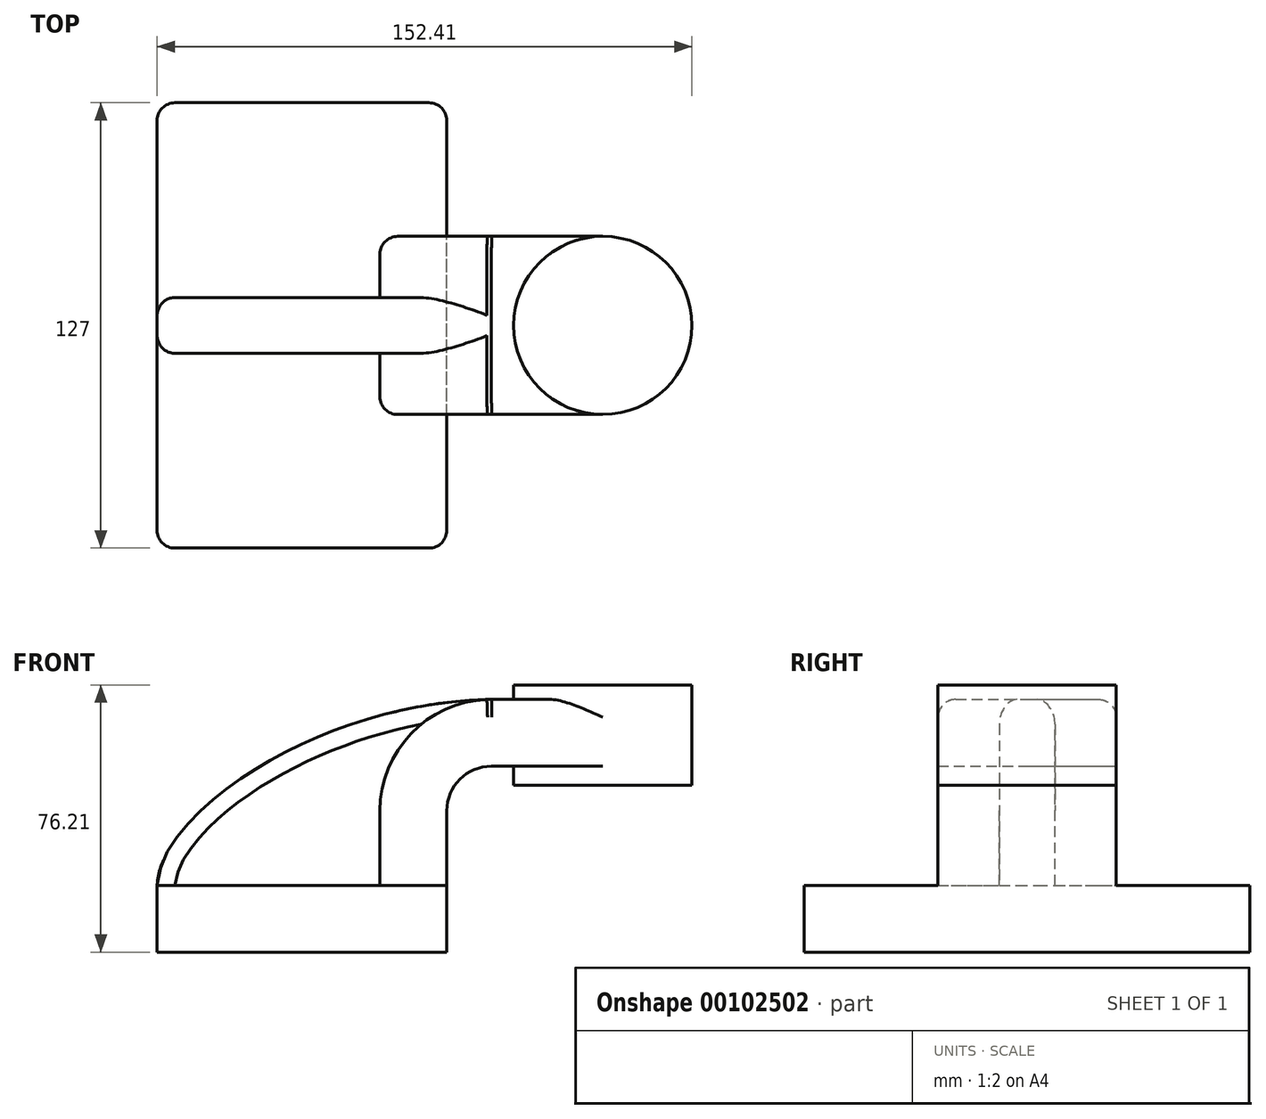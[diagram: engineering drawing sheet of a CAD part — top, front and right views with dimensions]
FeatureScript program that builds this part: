
annotation { "Feature Type Name" : "Feature", "Feature Type Description" : "" }
export const myFeature = defineFeature(function(context is Context, id is Id, definition is map)
    precondition{}
    {
        {
            var Q0;
            Q0=qCreatedBy(makeId("Front.planeOp"),FACE);
            var sketch = newSketch(context, id + "F0", { "sketchPlane" : qUnion([Q0])});
            skLineSegment(sketch, "E0.bottom", {"start": v(41.28, -9.52) * mm, "end": v(-41.28, -9.53) * mm});
            skLineSegment(sketch, "E0.top", {"start": v(41.28, 9.53) * mm, "end": v(-41.28, 9.53) * mm});
            skLineSegment(sketch, "E0.left", {"start": v(41.28, -9.52) * mm, "end": v(41.28, 9.53) * mm});
            skLineSegment(sketch, "E0.right", {"start": v(-41.28, -9.53) * mm, "end": v(-41.28, 9.53) * mm});
            skPoint(sketch, "E0.middle", {"position": v(0, 0) * mm});
            skLineSegment(sketch, "E1.bottom", {"start": v(111.12, 38.1) * mm, "end": v(60.33, 38.1) * mm});
            skLineSegment(sketch, "E1.top", {"start": v(111.12, 66.68) * mm, "end": v(60.33, 66.68) * mm});
            skLineSegment(sketch, "E1.left", {"start": v(111.12, 38.1) * mm, "end": v(111.12, 66.68) * mm});
            skLineSegment(sketch, "E1.right", {"start": v(60.33, 38.1) * mm, "end": v(60.33, 66.68) * mm});
            skPoint(sketch, "E1.middle", {"position": v(85.72, 52.39) * mm});
            skLineSegment(sketch, "E2", {"start": v(41.28, 9.53) * mm, "end": v(41.28, 30.76) * mm});
            skLineSegment(sketch, "E3", {"start": v(85.72, 43.49) * mm, "end": v(54, 43.49) * mm});
            skArc(sketch, "E4", {"start": v(41.28, 30.76) * mm, "mid": v(45, 39.76) * mm, "end": v(54, 43.49) * mm});
            skLineSegment(sketch, "E5.0", {"start": v(22.23, 9.53) * mm, "end": v(22.23, 30.76) * mm});
            skArc(sketch, "E5.1", {"start": v(22.23, 30.76) * mm, "mid": v(31.53, 53.23) * mm, "end": v(54, 62.54) * mm});
            skLineSegment(sketch, "E5.2", {"start": v(85.72, 62.54) * mm, "end": v(54, 62.54) * mm});
            skLineSegment(sketch, "E6", {"start": v(85.72, 38.1) * mm, "end": v(85.72, 66.68) * mm});
            skFitSpline(sketch, "E7", {"points": [v(-41.28, 9.53) * mm, v(54, 62.54) * mm], "startDerivative": vector(2.14, 63.8) * mm, "endDerivative": vector(144.8, 2.14) * mm});
            skSolve(sketch);
        }
        {
            var Q0;
            Q0=makeQuery(id+"F0.imprint","IMPRINT",FACE,{"disambiguationData":[TD([[makeQuery(id+"F0.imprint","IMPRINT",EDGE,{"derivedFrom":sQuery(id+"F0.wireOp",EDGE,"E0.bottom")}),-1.0]])]});
            extrude(context, id + "F1", {"entities" : qUnion([Q0]), "endBound" : BoundingType.SYMMETRIC, "depth" : 127 * mm});
        }
        {
            var Q0;
            {var subQ9=sQuery(id+"F0.wireOp",EDGE,"E2");Q0=makeQuery(id+"F0.imprint","IMPRINT",FACE,{"disambiguationData":[TD([[makeQuery(id+"F0.imprint","IMPRINT",EDGE,{"derivedFrom":subQ9}),1.0]])]});}
            var Q1;
            {var subQ0=sQuery(id+"F0.wireOp",EDGE,"E3");var subQ1=sQuery(id+"F0.wireOp",EDGE,"E1.right");var subQ2=makeQuery(id+"F0.imprint","INTERSECT",VERTEX,{"derivedFrom":[subQ1,subQ0]});Q1=makeQuery(id+"F0.imprint","IMPRINT",FACE,{"disambiguationData":[TD([[makeQuery(id+"F0.imprint","IMPRINT",EDGE,{"disambiguationData":[TD([[subQ2,-1.0]])],"derivedFrom":subQ1}),-1.0]])]});}
            extrude(context, id + "F2", {"entities" : qUnion([Q0, Q1]), "operationType" : NewBodyOperationType.ADD, "endBound" : BoundingType.SYMMETRIC, "depth" : 50.8 * mm});
        }
        {
            var Q0;
            {var subQ3=sQuery(id+"F0.wireOp",EDGE,"E5.0");Q0=makeQuery(id+"F0.imprint","IMPRINT",FACE,{"disambiguationData":[TD([[makeQuery(id+"F0.imprint","IMPRINT",EDGE,{"derivedFrom":subQ3}),1.0]])]});}
            extrude(context, id + "F3", {"entities" : qUnion([Q0]), "operationType" : NewBodyOperationType.ADD, "endBound" : BoundingType.SYMMETRIC, "depth" : 15.88 * mm});
        }
        {
            var Q0;
            {var subQ0=sQuery(id+"F0.wireOp",EDGE,"E1.left");Q0=makeQuery(id+"F0.imprint","IMPRINT",FACE,{"disambiguationData":[TD([[makeQuery(id+"F0.imprint","IMPRINT",EDGE,{"derivedFrom":subQ0}),1.0]])]});}
            var Q1;
            Q1=sQuery(id+"F0.wireOp",EDGE,"E6");
            revolve(context, id + "F4", {"operationType" : NewBodyOperationType.ADD, "entities" : qUnion([Q0]), "axis" : qUnion([Q1]), "revolveType" : RevolveType.FULL});
        }
        {
            var Q0;
            Q0=makeQuery(id+"F1.opExtrude","CAP_EDGE",EDGE,{"disambiguationData":[OSD([sQuery(id+"F0.wireOp",EDGE,"E0.left")])],"isStart":false});
            var Q1;
            Q1=makeQuery(id+"F1.opExtrude","CAP_EDGE",EDGE,{"disambiguationData":[OSD([sQuery(id+"F0.wireOp",EDGE,"E0.right")])],"isStart":false});
            var Q2;
            Q2=makeQuery(id+"F1.opExtrude","CAP_EDGE",EDGE,{"disambiguationData":[OSD([sQuery(id+"F0.wireOp",EDGE,"E0.left")])],"isStart":true});
            var Q3;
            Q3=makeQuery(id+"F1.opExtrude","CAP_EDGE",EDGE,{"disambiguationData":[OSD([sQuery(id+"F0.wireOp",EDGE,"E0.right")])],"isStart":true});
            var Q4;
            Q4=makeQuery(id+"F3.opExtrude","CAP_EDGE",EDGE,{"disambiguationData":[OSD([sQuery(id+"F0.wireOp",EDGE,"E7")])],"isStart":false});
            var Q5;
            Q5=makeQuery(id+"F3.opExtrude","CAP_EDGE",EDGE,{"disambiguationData":[OSD([sQuery(id+"F0.wireOp",EDGE,"E7")])],"isStart":true});
            var Q6;
            Q6=makeQuery(id+"F2.opExtrude","CAP_EDGE",EDGE,{"disambiguationData":[OSD([sQuery(id+"F0.wireOp",EDGE,"E5.2")])],"isStart":false});
            var Q7;
            Q7=makeQuery(id+"F2.opExtrude","CAP_EDGE",EDGE,{"disambiguationData":[OSD([sQuery(id+"F0.wireOp",EDGE,"E5.1")])],"isStart":false});
            var Q8;
            Q8=makeQuery(id+"F2.opExtrude","CAP_EDGE",EDGE,{"disambiguationData":[OSD([sQuery(id+"F0.wireOp",EDGE,"E7")])],"isStart":false});
            var Q9;
            Q9=makeQuery(id+"F2.opExtrude","CAP_EDGE",EDGE,{"disambiguationData":[OSD([sQuery(id+"F0.wireOp",EDGE,"E5.0")])],"isStart":false});
            var Q10;
            Q10=makeQuery(id+"F2.opExtrude","CAP_EDGE",EDGE,{"disambiguationData":[OSD([sQuery(id+"F0.wireOp",EDGE,"E5.0")])],"isStart":true});
            var Q11;
            Q11=makeQuery(id+"F2.opExtrude","CAP_EDGE",EDGE,{"disambiguationData":[OSD([sQuery(id+"F0.wireOp",EDGE,"E5.1")])],"isStart":true});
            var Q12;
            Q12=makeQuery(id+"F2.opExtrude","CAP_EDGE",EDGE,{"disambiguationData":[OSD([sQuery(id+"F0.wireOp",EDGE,"E7")])],"isStart":true});
            var Q13;
            Q13=makeQuery(id+"F2.opExtrude","CAP_EDGE",EDGE,{"disambiguationData":[OSD([sQuery(id+"F0.wireOp",EDGE,"E5.2")])],"isStart":true});
            fillet(context, id + "F5", {"entities" : qUnion([Q0, Q1, Q2, Q3, Q4, Q5, Q6, Q7, Q8, Q9, Q10, Q11, Q12, Q13]), "radius" : 5.08 * mm, "tangentPropagation" : true, "allowEdgeOverflow" : false});
        }
    });
